# Revit family: Gira_5001003
name_source: partatom
category: Elektroinstallationen
revit_build: Autodesk Revit 2017 (Build: 20160225_1515(x64)
units: mm (PartAtom-declared; Revit-internal decimal feet)

## family parameters
Basisbauteil = Fläche
Beim Laden mit Abzugskörper schneiden = Nein
Bemaßung runder Anschluss = Durchmesser verwenden
Beschriftungsausrichtung beibehalten = Nein
Gemeinsam genutzt = Nein
Raumberechnungspunkt = Nein
Teiletyp = Normal

## types (1)
- KNX Tastsens.4 Komfort 1f TS4 Weiß
    Andere Bussysteme = ohne
    Anzahl der Betätigungspunkte = 0
    Anzahl der Tasten = 1
    BIM = https://media.stage.bim.site TS4 1fach.rfa
    BIMSITE_PRODUCT_ID = c639142d951a84f3599d7fd122a1e332b6d742c8
    Beschreibung = KNX Tastsensor 4 Komfort 1fach   Weiß Merkmale:  Tastsensor mit integriertem Busankoppler und der Möglichkeit einen verdrahteten Fernfühler anzuschließen.  Wippen- oder Tastenfunktion für jede Bedienfläche einstellbar.  Funktionen: Schalten, Dimmen, Jalousie, Wertgeber, Szenennebenstelle, 2-Kanal-Bedienung und Reglernebenstelle.  Schalten: Reaktion beim Drücken und   oder Loslassen, Einschalten, Ausschalten, Umschalten.  Dimmen: Zeiten für kurze und lange Betätigung, Dimmen in verschiedenen Stufen, Telegrammwiederholung bei langer Betätigung, Senden eines Stopptelegramms bei Ende der Betätigung.  Jalousiesteuerung: vier verschiedene Bedienkonzepte mit Zeiten für kurze und lange Betätigung und Lamellenverstellung.  Wertgeberfunktion: Wahl des Wertebereichs, Wert bei Betätigung.  Szenennebenstelle: mit oder ohne Speicherfunktion, Abruf interne Szene mit oder ohne Speicherfunktion.  2-Kanal-Bedienung: Für jede Wippe oder jede Taste kann die Bedienung von zwei unabhängigen Kanälen eingestellt werden. Dadurch können durch einen Tastendruck bis zu zwei Telegramme auf den Bus gesendet werden. Die Kanäle können unabhängig voneinander auf die Funktionen Schalten, Wertgeber oder Szene aufrufen parametriert werden. Reglernebenstelle- Eigenschaften:  Durch die Tastsensorfunktion Reglernebenstelle können externe Raumtemperaturregler angesteuert werden.  Betriebsmodusumschaltung, Zwang-Betriebsmodusumschaltung, Präsenzfunktion und Sollwertverschiebung.  Auswertung des Reglerzustandes über die Status-LED. Funktionen der Status-LED:  Jede Status-LED kann unabhängig zur Bedienfläche parametriert werden.  Die Status-LED können wahlweise rot, grün, blau, gelb, cyan, orange, violett oder weiß leuchten.  Funktionen Status-LED: immer AUS, immer EIN, Betätigungsanzeige, Telegrammquittierung, Statusanzeige, invertierte Statusanzeige, Ansteuerung über separates LED-Objekt, Betriebsmodusanzeige, Anzeige Reglerstatus, Anzeige Präsenzstatus und Anzeige invertierter Präsenzstatus.  Zusätzlich kann für jede Status-LED eine überlagerte Funktion freigegeben werden, wodurch eine andere Farbe und Anzeigeart eingestellt werden kann. Allgemeine Funktionen:  LED Alarmmeldung: Sämtliche LED des Tastsensors können bei einer Alarmmeldung gleichzeitig rot blinken.  LED Orientierungsbeleuchtung: Zur Orientierung können alle LED dauerhaft ausgeschaltet oder eingeschaltet sein, den Status eines separaten Kommunikationsobjekts anzeigen (EIN, AUS, blinken) oder bei einem beliebigen Tastendruck eingeschaltet und nach Ablauf einer Verzögerungszeit automatisch wieder abgeschaltet werden.  LED Nachtabsenkung: Steuerung der Helligkeit aller Status-LED durch ein Kommunikationsobjekt. Dadurch ist beispielsweise das Reduzieren der Helligkeit während der Nachtstunden auf einen in der ETS konfigurierten Wert möglich.  Sperrfunktion zum Sperren von einzelnen Tasten- bzw. Wippen.  Szenenfunktion: Interne Speicherung von bis zu acht Szenen mit acht Ausgangskanälen.  Temperaturmessung: Raumtemperaturmessungen durch internen Fühler, internen und verdrahteten Fernfühler oder internen und externen Fühler.  Raumfeuchtemessung: Messung der Raumfeuchte durch internen Fühler.  Demontageschutz  Updatefähig und vorbereitet für KNX Secure.  Hinweise :  Professionelle Beschriftung über den Gira Beschriftungsservice www.beschriftung.gira.de.  Der Tastsensor wird mit einer programmneutralen Inbetriebnahme-Wippe geliefert. Das passende Wippenset zum Schalterprogramm ist separat zu bestellen.
    Bussystem Funkbus = Nein
    Bussystem KNX = Ja
    Bussystem KNX-Funk = Nein
    Bussystem LON = Nein
    Bussystem Powernet = Nein
    Datenblatt = https://media.stage.bim.site
    Datenblatt 1 = https://media.stage.bim.site
    Farbe = weiß
    Funk bidirektional = Nein
    GTIN = 4010337070870
    HAN = 5001003
    HeinzeBIM = https://www.heinze.de
    Hersteller = Gira
    Kosten = 0 $
    Mit Beschriftungsfeld = Nein
    Mit Busankopplung = Ja
    Mit Diebstahl-/Demontageschutz = Ja
    Mit Display = Nein
    Mit Infrarotsensor = Nein
    Mit LED-Anzeige = Ja
    Mit Raumthermostat = Nein
    Montageart = Unterputz
    Produktseite = https://media.stage.bim.site
    Schutzart (IP) = IP21
    Transparent = Nein
    Typname = KNX Tastsens.4 Komfort 1f TS4 Weiß
    URL = https://www.gira.de
    Vorgabe-Ansicht = 1219 mm
    White = White

## geometry (parser evidence)
native form markers: Sweep x3
no freeform markers — native parametric forms only
